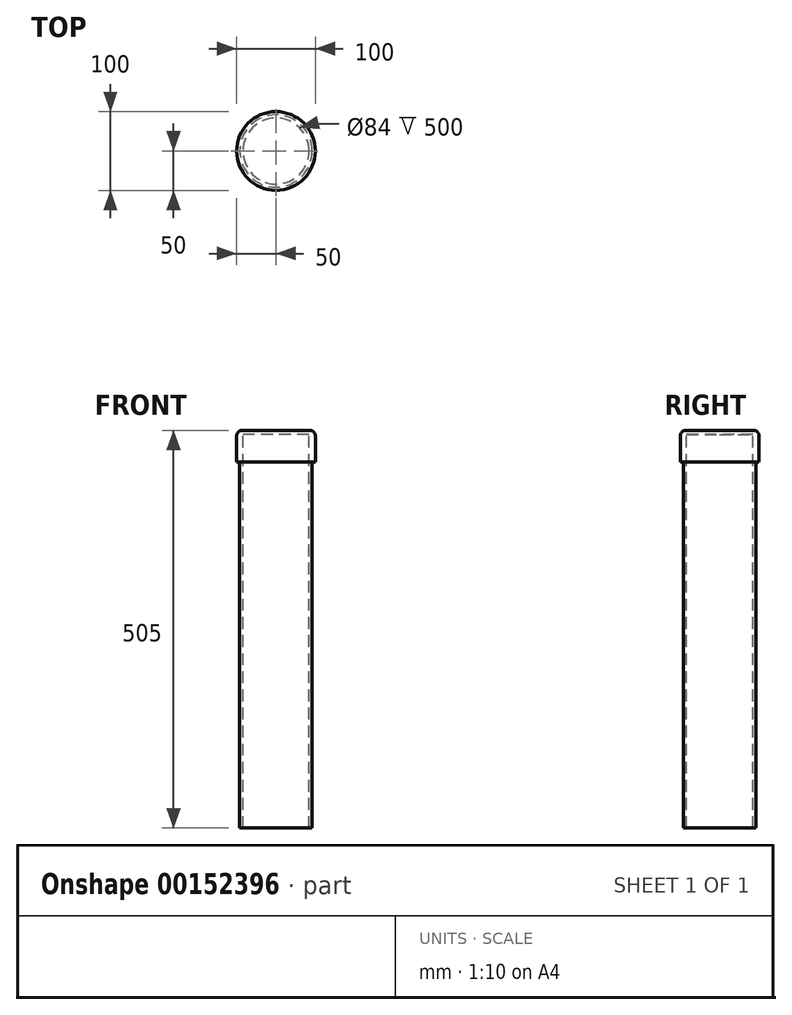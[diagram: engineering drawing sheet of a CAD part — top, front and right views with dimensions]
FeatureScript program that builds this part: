
annotation { "Feature Type Name" : "Feature", "Feature Type Description" : "" }
export const myFeature = defineFeature(function(context is Context, id is Id, definition is map)
    precondition{}
    {
        {
            var Q0;
            Q0=qCreatedBy(makeId("Top.planeOp"),FACE);
            var sketch = newSketch(context, id + "F0", { "sketchPlane" : qUnion([Q0])});
            skCircle(sketch, "E0", {"center": v(0, 0) * mm, "radius": 42 * mm});
            skCircle(sketch, "E1", {"center": v(0, 0) * mm, "radius": 46 * mm});
            skCircle(sketch, "E2", {"center": v(0, 0) * mm, "radius": 50 * mm});
            skSolve(sketch);
        }
        {
            var Q0;
            Q0=qSketchRegion(id+"F0",true);
            var Q1;
            Q1=makeQuery(id+"F0.imprint","IMPRINT",FACE,{"disambiguationData":[TD([[makeQuery(id+"F0.imprint","IMPRINT",EDGE,{"derivedFrom":sQuery(id+"F0.wireOp",EDGE,"E0")}),-1.0]])]});
            var Q2;
            Q2=makeQuery(id+"F0.imprint","IMPRINT",FACE,{"disambiguationData":[TD([[makeQuery(id+"F0.imprint","IMPRINT",EDGE,{"derivedFrom":sQuery(id+"F0.wireOp",EDGE,"E0")}),1.0]])]});
            extrude(context, id + "F1", {"entities" : qUnion([Q0, Q1, Q2]), "depth" : 5 * mm});
        }
        {
            var Q0;
            Q0=makeQuery(id+"F0.imprint","IMPRINT",FACE,{"disambiguationData":[TD([[makeQuery(id+"F0.imprint","IMPRINT",EDGE,{"derivedFrom":sQuery(id+"F0.wireOp",EDGE,"E0")}),-1.0]])]});
            extrude(context, id + "F2", {"entities" : qUnion([Q0]), "operationType" : NewBodyOperationType.ADD, "oppositeDirection" : true, "depth" : 500 * mm});
        }
        {
            var Q0;
            Q0=makeQuery(id+"F0.imprint","IMPRINT",FACE,{"disambiguationData":[TD([[makeQuery(id+"F0.imprint","IMPRINT",EDGE,{"derivedFrom":sQuery(id+"F0.wireOp",EDGE,"E1")}),-1.0]])]});
            extrude(context, id + "F3", {"entities" : qUnion([Q0]), "operationType" : NewBodyOperationType.ADD, "oppositeDirection" : true, "depth" : 35 * mm});
        }
        {
            var Q0;
            Q0=makeQuery(id+"F1.opExtrude","CAP_EDGE",EDGE,{"disambiguationData":[OSD([sQuery(id+"F0.wireOp",EDGE,"E2")])],"isStart":false});
            fillet(context, id + "F4", {"entities" : qUnion([Q0]), "radius" : 7 * mm, "tangentPropagation" : true, "allowEdgeOverflow" : false});
        }
    });
